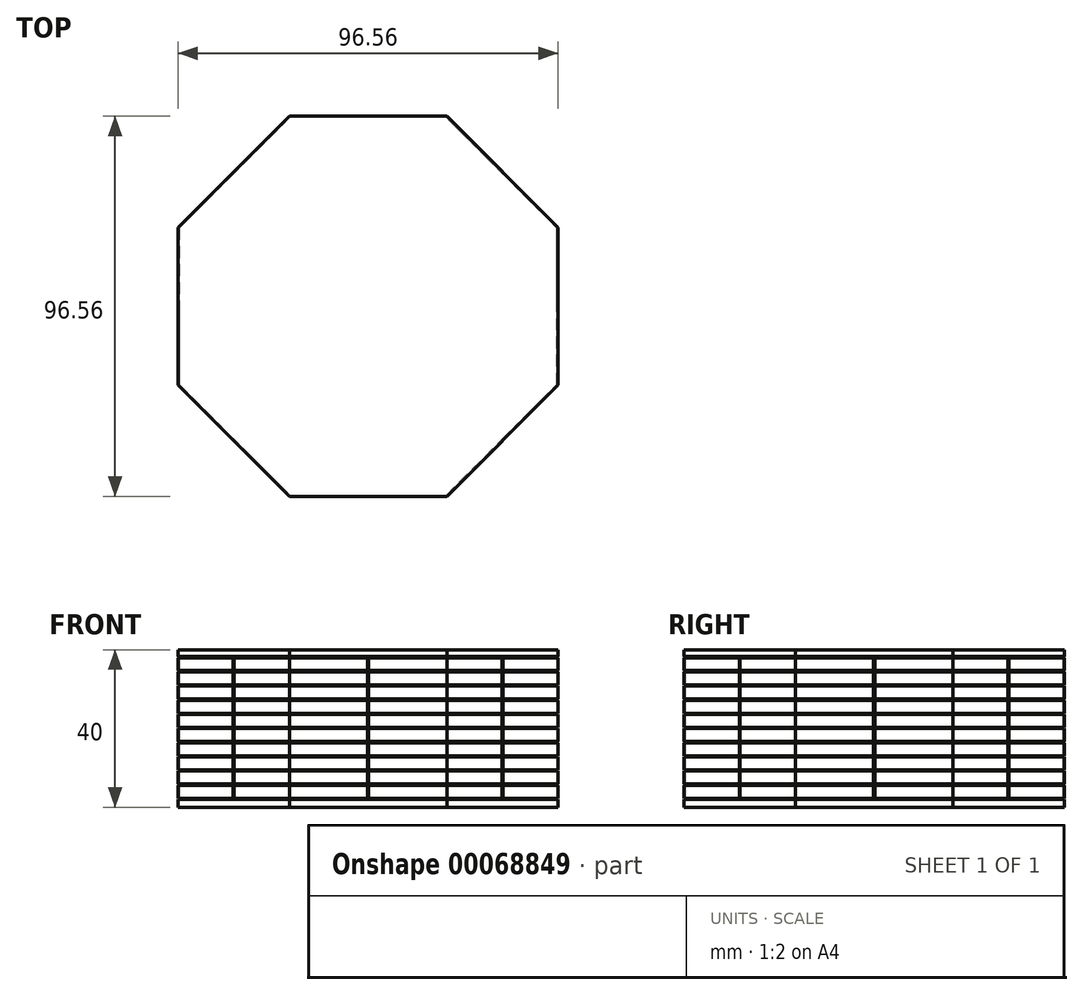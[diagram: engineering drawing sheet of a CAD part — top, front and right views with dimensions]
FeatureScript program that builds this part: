
annotation { "Feature Type Name" : "Feature", "Feature Type Description" : "" }
export const myFeature = defineFeature(function(context is Context, id is Id, definition is map)
    precondition{}
    {
        {
            var Q0;
            Q0=qCreatedBy(makeId("Top.planeOp"),FACE);
            var sketch = newSketch(context, id + "F0", { "sketchPlane" : qUnion([Q0])});
            skCircle(sketch, "E0.cCircle", {"center": v(0, 0) * mm, "radius": 48.28 * mm, "construction": true});
            skLineSegment(sketch, "E0.0", {"start": v(48.28, 20) * mm, "end": v(48.28, -20) * mm});
            skLineSegment(sketch, "E0.1", {"start": v(48.28, -20) * mm, "end": v(20, -48.28) * mm});
            skLineSegment(sketch, "E0.2", {"start": v(20, -48.28) * mm, "end": v(-20, -48.28) * mm});
            skLineSegment(sketch, "E0.3", {"start": v(-20, -48.28) * mm, "end": v(-48.28, -20) * mm});
            skLineSegment(sketch, "E0.4", {"start": v(-48.28, -20) * mm, "end": v(-48.28, 20) * mm});
            skLineSegment(sketch, "E0.5", {"start": v(-48.28, 20) * mm, "end": v(-20, 48.28) * mm});
            skLineSegment(sketch, "E0.6", {"start": v(-20, 48.28) * mm, "end": v(20, 48.28) * mm});
            skLineSegment(sketch, "E0.7", {"start": v(20, 48.28) * mm, "end": v(48.28, 20) * mm});
            skPoint(sketch, "E0.0.midPoint", {"position": v(48.28, 0) * mm});
            skSolve(sketch);
        }
        {
            var Q0;
            Q0=qCreatedBy(makeId("Top.planeOp"),FACE);
            var sketch = newSketch(context, id + "F1", { "sketchPlane" : qUnion([Q0])});
            skLineSegment(sketch, "E1", {"start": v(-48.02, 0) * mm, "end": v(-48.28, 0.15) * mm});
            skLineSegment(sketch, "E2", {"start": v(-48.28, 0.15) * mm, "end": v(-48.28, -0.15) * mm});
            skLineSegment(sketch, "E3", {"start": v(-48.28, -0.15) * mm, "end": v(-48.02, 0) * mm});
            skLineSegment(sketch, "E4.1.0", {"start": v(-34.25, -34.04) * mm, "end": v(-34.04, -34.25) * mm});
            skLineSegment(sketch, "E4.1.1", {"start": v(-34.04, -34.25) * mm, "end": v(-33.96, -33.96) * mm});
            skLineSegment(sketch, "E4.1.2", {"start": v(-33.96, -33.96) * mm, "end": v(-34.25, -34.04) * mm});
            skLineSegment(sketch, "E4.2.0", {"start": v(-0.15, -48.28) * mm, "end": v(0.15, -48.28) * mm});
            skLineSegment(sketch, "E4.2.1", {"start": v(0.15, -48.28) * mm, "end": v(0, -48.02) * mm});
            skLineSegment(sketch, "E4.2.2", {"start": v(0, -48.02) * mm, "end": v(-0.15, -48.28) * mm});
            skLineSegment(sketch, "E4.3.0", {"start": v(34.04, -34.25) * mm, "end": v(34.25, -34.04) * mm});
            skLineSegment(sketch, "E4.3.1", {"start": v(34.25, -34.04) * mm, "end": v(33.96, -33.96) * mm});
            skLineSegment(sketch, "E4.3.2", {"start": v(33.96, -33.96) * mm, "end": v(34.04, -34.25) * mm});
            skLineSegment(sketch, "E4.4.0", {"start": v(48.28, -0.15) * mm, "end": v(48.28, 0.15) * mm});
            skLineSegment(sketch, "E4.4.1", {"start": v(48.28, 0.15) * mm, "end": v(48.02, 0) * mm});
            skLineSegment(sketch, "E4.4.2", {"start": v(48.02, 0) * mm, "end": v(48.28, -0.15) * mm});
            skLineSegment(sketch, "E4.5.0", {"start": v(34.25, 34.04) * mm, "end": v(34.04, 34.25) * mm});
            skLineSegment(sketch, "E4.5.1", {"start": v(34.04, 34.25) * mm, "end": v(33.96, 33.96) * mm});
            skLineSegment(sketch, "E4.5.2", {"start": v(33.96, 33.96) * mm, "end": v(34.25, 34.04) * mm});
            skLineSegment(sketch, "E4.6.0", {"start": v(0.15, 48.28) * mm, "end": v(-0.15, 48.28) * mm});
            skLineSegment(sketch, "E4.6.1", {"start": v(-0.15, 48.28) * mm, "end": v(0, 48.02) * mm});
            skLineSegment(sketch, "E4.6.2", {"start": v(0, 48.02) * mm, "end": v(0.15, 48.28) * mm});
            skLineSegment(sketch, "E4.7.0", {"start": v(-34.04, 34.25) * mm, "end": v(-34.25, 34.04) * mm});
            skLineSegment(sketch, "E4.7.1", {"start": v(-34.25, 34.04) * mm, "end": v(-33.96, 33.96) * mm});
            skLineSegment(sketch, "E4.7.2", {"start": v(-33.96, 33.96) * mm, "end": v(-34.04, 34.25) * mm});
            skPoint(sketch, "E4.center", {"position": v(0, 0) * mm});
            skSolve(sketch);
        }
        {
            var Q0;
            Q0 = qSketchRegion(id + "F0", true);
            extrude(context, id + "F2", {"entities" : qUnion([Q0]), "depth" : 40 * mm});
        }
        {
            var Q0;
            Q0 = qSketchRegion(id + "F1", true);
            extrude(context, id + "F3", {"entities" : qUnion([Q0]), "operationType" : NewBodyOperationType.REMOVE, "depth" : 38 * mm, "hasSecondDirection" : true, "secondDirectionOppositeDirection" : false, "secondDirectionDepth" : 2 * mm});
        }
        {
            var Q0;
            Q0=qCreatedBy(makeId("Front.planeOp"),FACE);
            var sketch = newSketch(context, id + "F4", { "sketchPlane" : qUnion([Q0])});
            skLineSegment(sketch, "E5", {"start": v(-48.28, 2.3) * mm, "end": v(-48.02, 2.15) * mm});
            skLineSegment(sketch, "E6", {"start": v(-48.02, 2.15) * mm, "end": v(-48.28, 2) * mm});
            skLineSegment(sketch, "E7", {"start": v(-48.28, 2) * mm, "end": v(-48.28, 2.3) * mm});
            skLineSegment(sketch, "E8.0.1.0", {"start": v(-48.28, 5.9) * mm, "end": v(-48.02, 5.75) * mm});
            skLineSegment(sketch, "E8.0.1.1", {"start": v(-48.02, 5.75) * mm, "end": v(-48.28, 5.6) * mm});
            skLineSegment(sketch, "E8.0.1.2", {"start": v(-48.28, 5.6) * mm, "end": v(-48.28, 5.9) * mm});
            skLineSegment(sketch, "E8.0.2.0", {"start": v(-48.28, 9.5) * mm, "end": v(-48.02, 9.35) * mm});
            skLineSegment(sketch, "E8.0.2.1", {"start": v(-48.02, 9.35) * mm, "end": v(-48.28, 9.2) * mm});
            skLineSegment(sketch, "E8.0.2.2", {"start": v(-48.28, 9.2) * mm, "end": v(-48.28, 9.5) * mm});
            skLineSegment(sketch, "E8.0.3.0", {"start": v(-48.28, 13.1) * mm, "end": v(-48.02, 12.95) * mm});
            skLineSegment(sketch, "E8.0.3.1", {"start": v(-48.02, 12.95) * mm, "end": v(-48.28, 12.8) * mm});
            skLineSegment(sketch, "E8.0.3.2", {"start": v(-48.28, 12.8) * mm, "end": v(-48.28, 13.1) * mm});
            skLineSegment(sketch, "E8.0.4.0", {"start": v(-48.28, 16.7) * mm, "end": v(-48.02, 16.55) * mm});
            skLineSegment(sketch, "E8.0.4.1", {"start": v(-48.02, 16.55) * mm, "end": v(-48.28, 16.4) * mm});
            skLineSegment(sketch, "E8.0.4.2", {"start": v(-48.28, 16.4) * mm, "end": v(-48.28, 16.7) * mm});
            skLineSegment(sketch, "E8.0.5.0", {"start": v(-48.28, 20.3) * mm, "end": v(-48.02, 20.15) * mm});
            skLineSegment(sketch, "E8.0.5.1", {"start": v(-48.02, 20.15) * mm, "end": v(-48.28, 20) * mm});
            skLineSegment(sketch, "E8.0.5.2", {"start": v(-48.28, 20) * mm, "end": v(-48.28, 20.3) * mm});
            skLineSegment(sketch, "E8.0.6.0", {"start": v(-48.28, 23.9) * mm, "end": v(-48.02, 23.75) * mm});
            skLineSegment(sketch, "E8.0.6.1", {"start": v(-48.02, 23.75) * mm, "end": v(-48.28, 23.6) * mm});
            skLineSegment(sketch, "E8.0.6.2", {"start": v(-48.28, 23.6) * mm, "end": v(-48.28, 23.9) * mm});
            skLineSegment(sketch, "E8.0.7.0", {"start": v(-48.28, 27.5) * mm, "end": v(-48.02, 27.35) * mm});
            skLineSegment(sketch, "E8.0.7.1", {"start": v(-48.02, 27.35) * mm, "end": v(-48.28, 27.2) * mm});
            skLineSegment(sketch, "E8.0.7.2", {"start": v(-48.28, 27.2) * mm, "end": v(-48.28, 27.5) * mm});
            skLineSegment(sketch, "E8.0.8.0", {"start": v(-48.28, 31.1) * mm, "end": v(-48.02, 30.95) * mm});
            skLineSegment(sketch, "E8.0.8.1", {"start": v(-48.02, 30.95) * mm, "end": v(-48.28, 30.8) * mm});
            skLineSegment(sketch, "E8.0.8.2", {"start": v(-48.28, 30.8) * mm, "end": v(-48.28, 31.1) * mm});
            skLineSegment(sketch, "E8.0.9.0", {"start": v(-48.28, 34.7) * mm, "end": v(-48.02, 34.55) * mm});
            skLineSegment(sketch, "E8.0.9.1", {"start": v(-48.02, 34.55) * mm, "end": v(-48.28, 34.4) * mm});
            skLineSegment(sketch, "E8.0.9.2", {"start": v(-48.28, 34.4) * mm, "end": v(-48.28, 34.7) * mm});
            skLineSegment(sketch, "E8.direction1", {"start": v(-48.28, 2.3) * mm, "end": v(-23.28, 2.3) * mm, "construction": true});
            skLineSegment(sketch, "E8.direction2", {"start": v(-48.28, 2.3) * mm, "end": v(-48.28, 5.9) * mm, "construction": true});
            skLineSegment(sketch, "E9.0.0.10", {"start": v(-48.28, 38.3) * mm, "end": v(-48.02, 38.15) * mm});
            skLineSegment(sketch, "E9.3.0.10", {"start": v(-48.02, 38.15) * mm, "end": v(-48.28, 38) * mm});
            skLineSegment(sketch, "E9.6.0.10", {"start": v(-48.28, 38) * mm, "end": v(-48.28, 38.3) * mm});
            skSolve(sketch);
        }
        {
            var Q0;
            Q0=makeQuery(id+"F3.boolean.opBoolean","COPY",FACE,{"derivedFrom":makeQuery(id+"F3.opExtrude","CAP_FACE",FACE,{"disambiguationData":[OSD([sQuery(id+"F1.wireOp",EDGE,"E1"),sQuery(id+"F1.wireOp",EDGE,"E2"),sQuery(id+"F1.wireOp",EDGE,"E3")])],"isStart":true})});
            var sketch = newSketch(context, id + "F5", { "sketchPlane" : qUnion([Q0])});
            skLineSegment(sketch, "E10.0", {"start": v(-48.28, -20) * mm, "end": v(-48.28, 20) * mm});
            skLineSegment(sketch, "E10.1", {"start": v(-48.28, 20) * mm, "end": v(-20, 48.28) * mm});
            skLineSegment(sketch, "E10.2", {"start": v(-20, 48.28) * mm, "end": v(20, 48.28) * mm});
            skLineSegment(sketch, "E10.3", {"start": v(20, 48.28) * mm, "end": v(48.28, 20) * mm});
            skLineSegment(sketch, "E10.4", {"start": v(48.28, 20) * mm, "end": v(48.28, -20) * mm});
            skLineSegment(sketch, "E10.5", {"start": v(48.28, -20) * mm, "end": v(20, -48.28) * mm});
            skLineSegment(sketch, "E10.6", {"start": v(-20, -48.28) * mm, "end": v(-48.28, -20) * mm});
            skLineSegment(sketch, "E10.7", {"start": v(20, -48.28) * mm, "end": v(-20, -48.28) * mm});
            skSolve(sketch);
        }
        {
            var Q0;
            Q0 = qSketchRegion(id + "F4", true);
            var Q1;
            Q1 = qConstructionFilter(qBodyType(qCreatedBy(id + "F5" ,EDGE), BodyType.WIRE), ConstructionObject.NO);
            sweep(context, id + "F6", {"operationType" : NewBodyOperationType.REMOVE, "profiles" : qUnion([Q0]), "path" : qUnion([Q1])});
        }
    });
